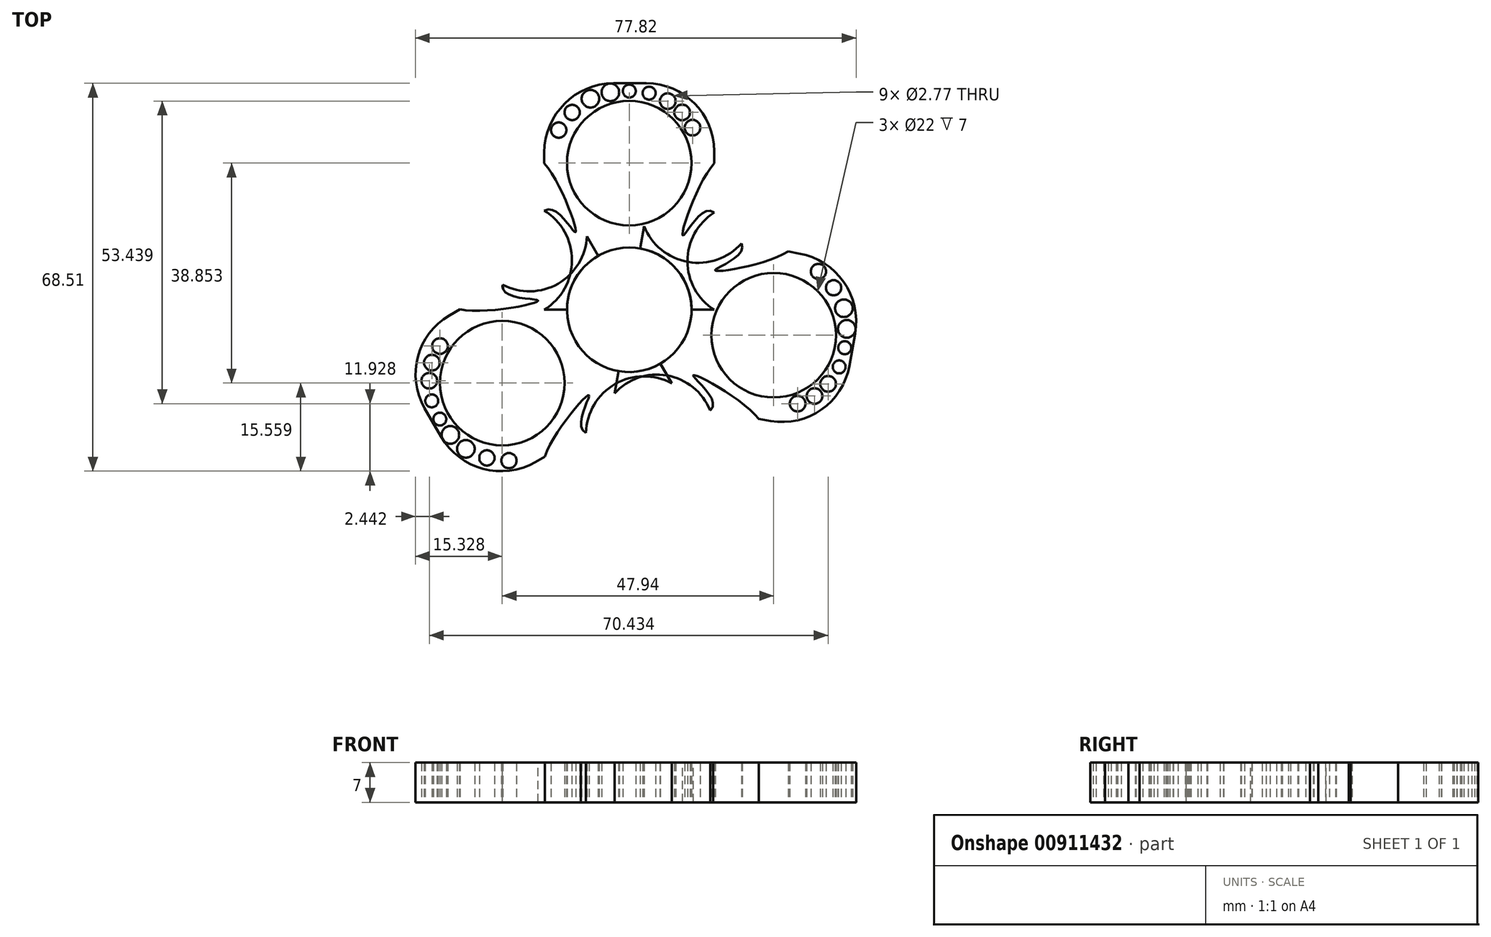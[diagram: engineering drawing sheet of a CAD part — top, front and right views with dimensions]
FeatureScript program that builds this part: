
annotation { "Feature Type Name" : "Feature", "Feature Type Description" : "" }
export const myFeature = defineFeature(function(context is Context, id is Id, definition is map)
    precondition{}
    {
        {
            var Q0;
            Q0=qCreatedBy(makeId("Top.planeOp"),FACE);
            var sketch = newSketch(context, id + "F0", { "sketchPlane" : qUnion([Q0])});
            skCircle(sketch, "E0", {"center": v(0, 0) * mm, "radius": 11 * mm});
            skLineSegment(sketch, "E1.bottom", {"start": v(0, 0) * mm, "end": v(15, 0) * mm});
            skLineSegment(sketch, "E1.top", {"start": v(0, 40) * mm, "end": v(3.02, 40) * mm});
            skLineSegment(sketch, "E1.left", {"start": v(0, 0) * mm, "end": v(0, 40) * mm});
            skLineSegment(sketch, "E1.right", {"start": v(15, 0) * mm, "end": v(15, 28.02) * mm});
            skLineSegment(sketch, "E2.bottom", {"start": v(0, 0) * mm, "end": v(-15, 0) * mm});
            skLineSegment(sketch, "E2.top", {"start": v(0, 40) * mm, "end": v(-2.77, 40) * mm});
            skLineSegment(sketch, "E2.right", {"start": v(-15, 0) * mm, "end": v(-15, 27.77) * mm});
            skLineSegment(sketch, "E3", {"start": v(0, 40) * mm, "end": v(0, 25.9) * mm});
            skCircle(sketch, "E4", {"center": v(0, 25.9) * mm, "radius": 11 * mm});
            skPoint(sketch, "E5.visualSharp", {"position": v(-15, 40) * mm});
            skArc(sketch, "E5.filletArc", {"start": v(-2.77, 40) * mm, "mid": v(-11.42, 36.42) * mm, "end": v(-15, 27.77) * mm});
            skPoint(sketch, "E6.visualSharp", {"position": v(15, 40) * mm});
            skArc(sketch, "E6.filletArc", {"start": v(15, 28.02) * mm, "mid": v(11.5, 36.5) * mm, "end": v(3.02, 40) * mm});
            skPoint(sketch, "E7.1.internal.snap0", {"position": v(-15, 13.88) * mm});
            skFitSpline(sketch, "E8", {"points": [v(-15, 25.86) * mm, v(-9.57, 13.73) * mm, v(-15, 17.51) * mm], "startDerivative": vector(15.03, -16.72) * mm, "endDerivative": vector(-15.82, -9.96) * mm});
            skFitSpline(sketch, "E9", {"points": [v(15, 25.86) * mm, v(9.53, 13.16) * mm, v(15, 17.15) * mm], "startDerivative": vector(-14.64, -15.58) * mm, "endDerivative": vector(14.98, -12.69) * mm});
            skPoint(sketch, "E10", {"position": v(15, 14) * mm});
            skCircle(sketch, "E11", {"center": v(-12.46, 31.73) * mm, "radius": 1.35 * mm});
            skCircle(sketch, "E12", {"center": v(-10.09, 34.86) * mm, "radius": 1.35 * mm});
            skCircle(sketch, "E13", {"center": v(-6.85, 37.29) * mm, "radius": 1.56 * mm});
            skCircle(sketch, "E14", {"center": v(-3.34, 38.42) * mm, "radius": 1.56 * mm});
            skCircle(sketch, "E15", {"center": v(0, 38.64) * mm, "radius": 1.14 * mm});
            skCircle(sketch, "E16", {"center": v(3.5, 38.26) * mm, "radius": 1.14 * mm});
            skCircle(sketch, "E17", {"center": v(6.8, 36.86) * mm, "radius": 1.38 * mm});
            skCircle(sketch, "E18", {"center": v(9.33, 34.86) * mm, "radius": 1.38 * mm});
            skCircle(sketch, "E19", {"center": v(11.17, 32.16) * mm, "radius": 1.38 * mm});
            skArc(sketch, "E20", {"start": v(-15, 0) * mm, "mid": v(-10.12, 8.76) * mm, "end": v(-15, 17.51) * mm});
            skArc(sketch, "E21", {"start": v(15, 17.15) * mm, "mid": v(10.27, 8.57) * mm, "end": v(15, 0) * mm});
            skSolve(sketch);
        }
        {
            var Q0;
            {var subQ0=sQuery(id+"F0.wireOp",EDGE,"E2.top");Q0=makeQuery(id+"F0.imprint","IMPRINT",FACE,{"disambiguationData":[TD([[makeQuery(id+"F0.imprint","IMPRINT",EDGE,{"derivedFrom":subQ0}),1.0]])]});}
            var Q1;
            {var subQ9=sQuery(id+"F0.wireOp",EDGE,"E1.top");Q1=makeQuery(id+"F0.imprint","IMPRINT",FACE,{"disambiguationData":[TD([[makeQuery(id+"F0.imprint","IMPRINT",EDGE,{"derivedFrom":subQ9}),-1.0]])]});}
            extrude(context, id + "F1", {"entities" : qUnion([Q0, Q1]), "depth" : 7 * mm, "offsetDistance" : 25 * mm});
        }
        {
            var Q0;
            Q0=qCreatedBy(makeId("Front.planeOp"),FACE);
            var sketch = newSketch(context, id + "F2", { "sketchPlane" : qUnion([Q0])});
            skLineSegment(sketch, "E22", {"start": v(0, 0) * mm, "end": v(0, 68.14) * mm});
            skSolve(sketch);
        }
        {
            var Q0;
            Q0=makeQuery(id+"F1.opExtrude","SWEPT_BODY",BODY,{"disambiguationData":[OSD([sQuery(id+"F0.wireOp",EDGE,"E0"),sQuery(id+"F0.wireOp",EDGE,"E1.bottom"),sQuery(id+"F0.wireOp",EDGE,"E1.top"),sQuery(id+"F0.wireOp",EDGE,"E1.right"),sQuery(id+"F0.wireOp",EDGE,"E2.bottom"),sQuery(id+"F0.wireOp",EDGE,"E2.top"),sQuery(id+"F0.wireOp",EDGE,"E2.right"),sQuery(id+"F0.wireOp",EDGE,"E4")])]});
            var Q1;
            Q1=sQuery(id+"F2.wireOp",EDGE,"E22");
            var Q2;
            Q2=sQuery(id+"F2.wireOp",EDGE,"E22");
            transform(context, id + "F3", {"entities" : qUnion([Q0]), "transformType" : TransformType.ROTATION, "transformAxis" : qUnion([Q2]), "angle" : 120 * degree, "makeCopy" : true});
        }
        {
            var Q0;
            Q0=makeQuery(id+"F3.opPattern","COPY",BODY,{"derivedFrom":makeQuery(id+"F1.opExtrude","SWEPT_BODY",BODY,{"disambiguationData":[OSD([sQuery(id+"F0.wireOp",EDGE,"E0"),sQuery(id+"F0.wireOp",EDGE,"E1.bottom"),sQuery(id+"F0.wireOp",EDGE,"E1.top"),sQuery(id+"F0.wireOp",EDGE,"E1.right"),sQuery(id+"F0.wireOp",EDGE,"E2.bottom"),sQuery(id+"F0.wireOp",EDGE,"E2.top"),sQuery(id+"F0.wireOp",EDGE,"E2.right"),sQuery(id+"F0.wireOp",EDGE,"E4")])]}),"instanceName":"1"});
            var Q1;
            Q1=sQuery(id+"F2.wireOp",EDGE,"E22");
            transform(context, id + "F4", {"entities" : qUnion([Q0]), "transformType" : TransformType.ROTATION, "transformAxis" : qUnion([Q1]), "angle" : 140 * degree, "makeCopy" : true});
        }
    });
